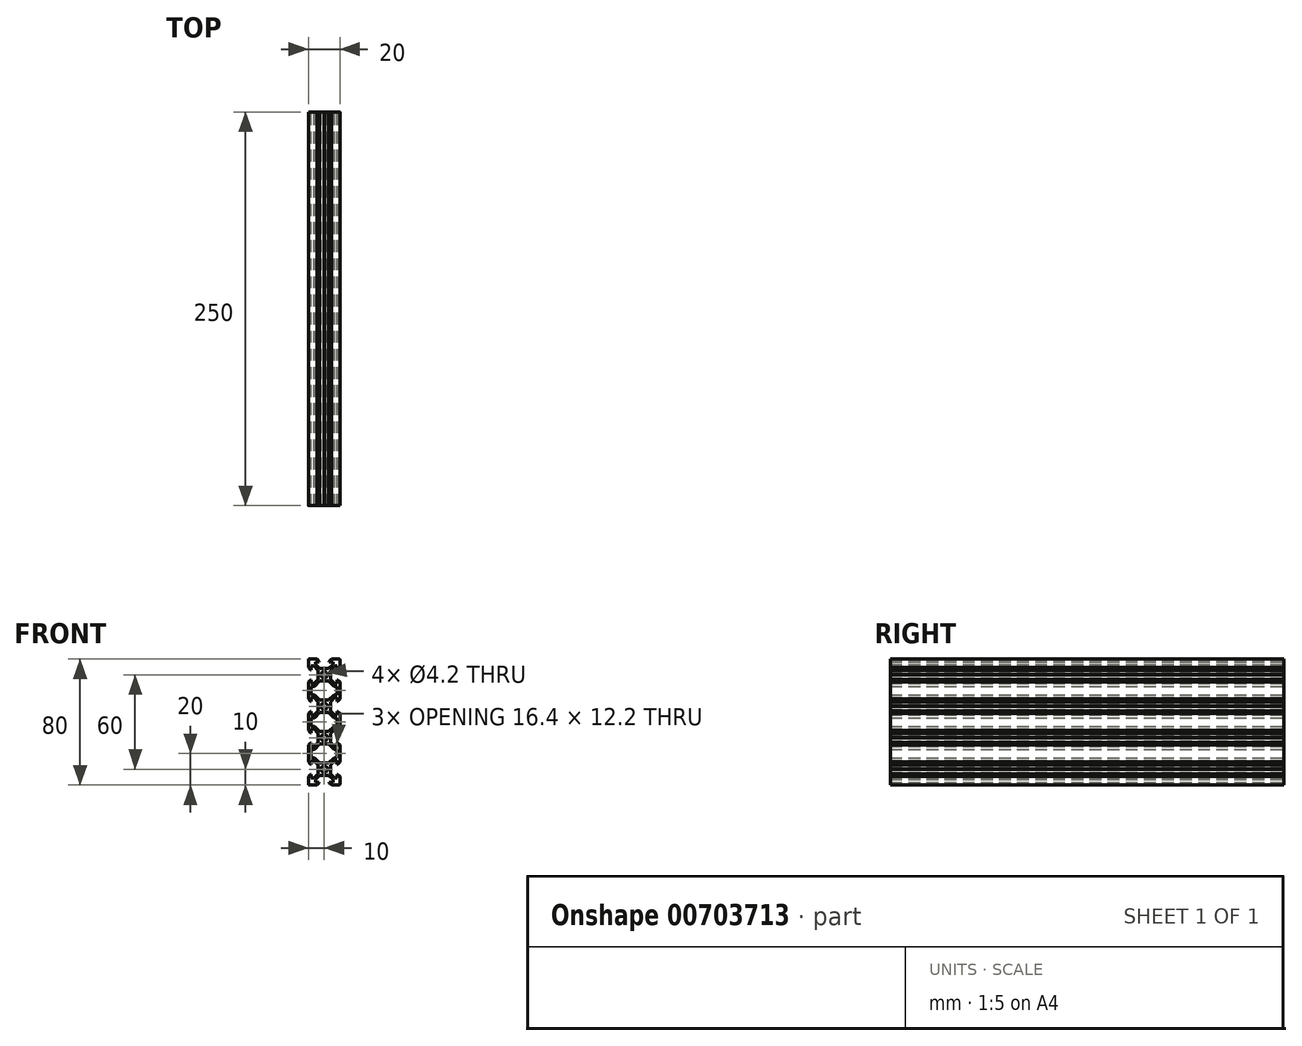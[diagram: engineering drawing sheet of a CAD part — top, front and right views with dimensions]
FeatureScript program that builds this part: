
annotation { "Feature Type Name" : "Feature", "Feature Type Description" : "" }
export const myFeature = defineFeature(function(context is Context, id is Id, definition is map)
    precondition{}
    {
        {
            var Q0;
            Q0=qCreatedBy(makeId("Front.planeOp"),FACE);
            var sketch = newSketch(context, id + "F0", { "sketchPlane" : qUnion([Q0])});
            skLineSegment(sketch, "E0", {"start": v(-3.9, 27.16) * mm, "end": v(-3.9, 29.79) * mm});
            skLineSegment(sketch, "E1", {"start": v(-6.56, 24.5) * mm, "end": v(-3.9, 27.16) * mm});
            skLineSegment(sketch, "E2", {"start": v(-8.2, 24.5) * mm, "end": v(-6.56, 24.5) * mm});
            skLineSegment(sketch, "E3", {"start": v(-8.2, 26.88) * mm, "end": v(-8.2, 24.5) * mm});
            skLineSegment(sketch, "E4", {"start": v(-8.54, 26.88) * mm, "end": v(-8.2, 26.88) * mm});
            skLineSegment(sketch, "E5", {"start": v(-10, 25.42) * mm, "end": v(-8.54, 26.88) * mm});
            skLineSegment(sketch, "E6", {"start": v(-10, 25.42) * mm, "end": v(-10, 14.58) * mm});
            skLineSegment(sketch, "E7", {"start": v(-10, 14.58) * mm, "end": v(-8.54, 13.12) * mm});
            skLineSegment(sketch, "E8", {"start": v(-8.54, 13.12) * mm, "end": v(-8.2, 13.12) * mm});
            skLineSegment(sketch, "E9", {"start": v(-8.2, 13.12) * mm, "end": v(-8.2, 15.5) * mm});
            skLineSegment(sketch, "E10", {"start": v(-8.2, 15.5) * mm, "end": v(-6.56, 15.5) * mm});
            skLineSegment(sketch, "E11", {"start": v(-6.56, 15.5) * mm, "end": v(-3.9, 12.84) * mm});
            skLineSegment(sketch, "E12", {"start": v(-3.9, 12.84) * mm, "end": v(-3.9, 10.21) * mm});
            skLineSegment(sketch, "E13", {"start": v(-3.9, 10.21) * mm, "end": v(-3.69, 10) * mm});
            skLineSegment(sketch, "E14", {"start": v(-3.9, 9.8) * mm, "end": v(-3.69, 10) * mm});
            skLineSegment(sketch, "E15", {"start": v(-3.9, 7.16) * mm, "end": v(-3.9, 9.8) * mm});
            skLineSegment(sketch, "E16", {"start": v(-6.56, 4.5) * mm, "end": v(-3.9, 7.16) * mm});
            skLineSegment(sketch, "E17", {"start": v(-8.2, 4.5) * mm, "end": v(-6.56, 4.5) * mm});
            skLineSegment(sketch, "E18", {"start": v(-8.2, 6.88) * mm, "end": v(-8.2, 4.5) * mm});
            skLineSegment(sketch, "E19", {"start": v(-8.54, 6.88) * mm, "end": v(-8.2, 6.88) * mm});
            skLineSegment(sketch, "E20", {"start": v(-10, 5.42) * mm, "end": v(-8.54, 6.88) * mm});
            skLineSegment(sketch, "E21", {"start": v(-10, 5.42) * mm, "end": v(-10, -5.42) * mm});
            skLineSegment(sketch, "E22", {"start": v(-10, -5.42) * mm, "end": v(-8.54, -6.88) * mm});
            skLineSegment(sketch, "E23", {"start": v(-8.54, -6.88) * mm, "end": v(-8.2, -6.88) * mm});
            skLineSegment(sketch, "E24", {"start": v(-8.2, -6.88) * mm, "end": v(-8.2, -4.5) * mm});
            skLineSegment(sketch, "E25", {"start": v(-8.2, -4.5) * mm, "end": v(-6.56, -4.5) * mm});
            skLineSegment(sketch, "E26", {"start": v(-6.56, -4.5) * mm, "end": v(-3.9, -7.16) * mm});
            skLineSegment(sketch, "E27", {"start": v(-3.9, -7.16) * mm, "end": v(-3.9, -9.8) * mm});
            skLineSegment(sketch, "E28", {"start": v(-3.9, -9.8) * mm, "end": v(-3.69, -10) * mm});
            skLineSegment(sketch, "E29", {"start": v(-3.9, -10.21) * mm, "end": v(-3.69, -10) * mm});
            skLineSegment(sketch, "E30", {"start": v(-3.9, -12.84) * mm, "end": v(-3.9, -10.21) * mm});
            skLineSegment(sketch, "E31", {"start": v(-6.56, -15.5) * mm, "end": v(-3.9, -12.84) * mm});
            skLineSegment(sketch, "E32", {"start": v(-8.2, -15.5) * mm, "end": v(-6.56, -15.5) * mm});
            skLineSegment(sketch, "E33", {"start": v(-8.2, -13.12) * mm, "end": v(-8.2, -15.5) * mm});
            skLineSegment(sketch, "E34", {"start": v(-8.54, -13.12) * mm, "end": v(-8.2, -13.12) * mm});
            skLineSegment(sketch, "E35", {"start": v(-10, -14.58) * mm, "end": v(-8.54, -13.12) * mm});
            skLineSegment(sketch, "E36", {"start": v(-10, -14.58) * mm, "end": v(-10, -25.42) * mm});
            skLineSegment(sketch, "E37", {"start": v(-10, -25.42) * mm, "end": v(-8.54, -26.88) * mm});
            skLineSegment(sketch, "E38", {"start": v(-8.54, -26.88) * mm, "end": v(-8.2, -26.88) * mm});
            skLineSegment(sketch, "E39", {"start": v(-8.2, -26.88) * mm, "end": v(-8.2, -24.5) * mm});
            skLineSegment(sketch, "E40", {"start": v(-8.2, -24.5) * mm, "end": v(-6.56, -24.5) * mm});
            skLineSegment(sketch, "E41", {"start": v(-6.56, -24.5) * mm, "end": v(-3.9, -27.16) * mm});
            skLineSegment(sketch, "E42", {"start": v(-3.9, -27.16) * mm, "end": v(-3.9, -29.79) * mm});
            skLineSegment(sketch, "E43", {"start": v(-3.9, -29.79) * mm, "end": v(-3.69, -30) * mm});
            skLineSegment(sketch, "E44", {"start": v(-3.9, -30.21) * mm, "end": v(-3.69, -30) * mm});
            skLineSegment(sketch, "E45", {"start": v(-3.9, -32.84) * mm, "end": v(-3.9, -30.21) * mm});
            skLineSegment(sketch, "E46", {"start": v(-6.56, -35.5) * mm, "end": v(-3.9, -32.84) * mm});
            skLineSegment(sketch, "E47", {"start": v(-8.2, -35.5) * mm, "end": v(-6.56, -35.5) * mm});
            skLineSegment(sketch, "E48", {"start": v(-8.2, -33.12) * mm, "end": v(-8.2, -35.5) * mm});
            skLineSegment(sketch, "E49", {"start": v(-8.54, -33.12) * mm, "end": v(-8.2, -33.12) * mm});
            skLineSegment(sketch, "E50", {"start": v(-10, -34.58) * mm, "end": v(-8.54, -33.12) * mm});
            skLineSegment(sketch, "E51", {"start": v(-10, -34.58) * mm, "end": v(-10, -39.5) * mm});
            skArc(sketch, "E52", {"start": v(-9.5, -40) * mm, "mid": v(-9.85, -39.85) * mm, "end": v(-10, -39.5) * mm});
            skLineSegment(sketch, "E53", {"start": v(-4.58, -40) * mm, "end": v(-9.5, -40) * mm});
            skLineSegment(sketch, "E54", {"start": v(-4.58, -40) * mm, "end": v(-3.12, -38.55) * mm});
            skLineSegment(sketch, "E55", {"start": v(-3.12, -38.55) * mm, "end": v(-3.12, -38.2) * mm});
            skLineSegment(sketch, "E56", {"start": v(-3.12, -38.2) * mm, "end": v(-5.5, -38.2) * mm});
            skLineSegment(sketch, "E57", {"start": v(-5.5, -38.2) * mm, "end": v(-5.5, -36.56) * mm});
            skLineSegment(sketch, "E58", {"start": v(-5.5, -36.56) * mm, "end": v(-2.84, -33.9) * mm});
            skLineSegment(sketch, "E59", {"start": v(-2.84, -33.9) * mm, "end": v(-0.21, -33.9) * mm});
            skLineSegment(sketch, "E60", {"start": v(-0.21, -33.9) * mm, "end": v(0, -33.69) * mm});
            skLineSegment(sketch, "E61", {"start": v(0.21, -33.9) * mm, "end": v(0, -33.69) * mm});
            skLineSegment(sketch, "E62", {"start": v(2.84, -33.9) * mm, "end": v(0.21, -33.9) * mm});
            skLineSegment(sketch, "E63", {"start": v(5.5, -36.56) * mm, "end": v(2.84, -33.9) * mm});
            skLineSegment(sketch, "E64", {"start": v(5.5, -38.2) * mm, "end": v(5.5, -36.56) * mm});
            skLineSegment(sketch, "E65", {"start": v(3.12, -38.2) * mm, "end": v(5.5, -38.2) * mm});
            skLineSegment(sketch, "E66", {"start": v(3.12, -38.55) * mm, "end": v(3.12, -38.2) * mm});
            skLineSegment(sketch, "E67", {"start": v(4.58, -40) * mm, "end": v(3.12, -38.55) * mm});
            skLineSegment(sketch, "E68", {"start": v(9.5, -40) * mm, "end": v(4.58, -40) * mm});
            skArc(sketch, "E69", {"start": v(10, -39.5) * mm, "mid": v(9.85, -39.85) * mm, "end": v(9.5, -40) * mm});
            skLineSegment(sketch, "E70", {"start": v(10, -34.58) * mm, "end": v(10, -39.5) * mm});
            skLineSegment(sketch, "E71", {"start": v(10, -34.58) * mm, "end": v(8.54, -33.12) * mm});
            skLineSegment(sketch, "E72", {"start": v(8.54, -33.12) * mm, "end": v(8.2, -33.12) * mm});
            skLineSegment(sketch, "E73", {"start": v(8.2, -33.12) * mm, "end": v(8.2, -35.5) * mm});
            skLineSegment(sketch, "E74", {"start": v(8.2, -35.5) * mm, "end": v(6.56, -35.5) * mm});
            skLineSegment(sketch, "E75", {"start": v(6.56, -35.5) * mm, "end": v(3.9, -32.84) * mm});
            skLineSegment(sketch, "E76", {"start": v(3.9, -32.84) * mm, "end": v(3.9, -30.21) * mm});
            skLineSegment(sketch, "E77", {"start": v(3.9, -30.21) * mm, "end": v(3.69, -30) * mm});
            skLineSegment(sketch, "E78", {"start": v(3.9, -29.79) * mm, "end": v(3.69, -30) * mm});
            skLineSegment(sketch, "E79", {"start": v(3.9, -27.16) * mm, "end": v(3.9, -29.79) * mm});
            skLineSegment(sketch, "E80", {"start": v(6.56, -24.5) * mm, "end": v(3.9, -27.16) * mm});
            skLineSegment(sketch, "E81", {"start": v(8.2, -24.5) * mm, "end": v(6.56, -24.5) * mm});
            skLineSegment(sketch, "E82", {"start": v(8.2, -26.88) * mm, "end": v(8.2, -24.5) * mm});
            skLineSegment(sketch, "E83", {"start": v(8.54, -26.88) * mm, "end": v(8.2, -26.88) * mm});
            skLineSegment(sketch, "E84", {"start": v(10, -25.42) * mm, "end": v(8.54, -26.88) * mm});
            skLineSegment(sketch, "E85", {"start": v(10, -14.58) * mm, "end": v(10, -25.42) * mm});
            skLineSegment(sketch, "E86", {"start": v(10, -14.58) * mm, "end": v(8.54, -13.12) * mm});
            skLineSegment(sketch, "E87", {"start": v(8.54, -13.12) * mm, "end": v(8.2, -13.12) * mm});
            skLineSegment(sketch, "E88", {"start": v(8.2, -13.12) * mm, "end": v(8.2, -15.5) * mm});
            skLineSegment(sketch, "E89", {"start": v(8.2, -15.5) * mm, "end": v(6.56, -15.5) * mm});
            skLineSegment(sketch, "E90", {"start": v(6.56, -15.5) * mm, "end": v(3.9, -12.84) * mm});
            skLineSegment(sketch, "E91", {"start": v(3.9, -12.84) * mm, "end": v(3.9, -10.21) * mm});
            skLineSegment(sketch, "E92", {"start": v(3.9, -10.21) * mm, "end": v(3.69, -10) * mm});
            skLineSegment(sketch, "E93", {"start": v(3.9, -9.8) * mm, "end": v(3.69, -10) * mm});
            skLineSegment(sketch, "E94", {"start": v(3.9, -7.16) * mm, "end": v(3.9, -9.8) * mm});
            skLineSegment(sketch, "E95", {"start": v(6.56, -4.5) * mm, "end": v(3.9, -7.16) * mm});
            skLineSegment(sketch, "E96", {"start": v(8.2, -4.5) * mm, "end": v(6.56, -4.5) * mm});
            skLineSegment(sketch, "E97", {"start": v(8.2, -6.88) * mm, "end": v(8.2, -4.5) * mm});
            skLineSegment(sketch, "E98", {"start": v(8.54, -6.88) * mm, "end": v(8.2, -6.88) * mm});
            skLineSegment(sketch, "E99", {"start": v(10, -5.42) * mm, "end": v(8.54, -6.88) * mm});
            skLineSegment(sketch, "E100", {"start": v(10, 5.42) * mm, "end": v(10, -5.42) * mm});
            skLineSegment(sketch, "E101", {"start": v(10, 5.42) * mm, "end": v(8.54, 6.88) * mm});
            skLineSegment(sketch, "E102", {"start": v(8.54, 6.88) * mm, "end": v(8.2, 6.88) * mm});
            skLineSegment(sketch, "E103", {"start": v(8.2, 6.88) * mm, "end": v(8.2, 4.5) * mm});
            skLineSegment(sketch, "E104", {"start": v(8.2, 4.5) * mm, "end": v(6.56, 4.5) * mm});
            skLineSegment(sketch, "E105", {"start": v(6.56, 4.5) * mm, "end": v(3.9, 7.16) * mm});
            skLineSegment(sketch, "E106", {"start": v(3.9, 7.16) * mm, "end": v(3.9, 9.8) * mm});
            skLineSegment(sketch, "E107", {"start": v(3.9, 9.8) * mm, "end": v(3.69, 10) * mm});
            skLineSegment(sketch, "E108", {"start": v(3.9, 10.21) * mm, "end": v(3.69, 10) * mm});
            skLineSegment(sketch, "E109", {"start": v(3.9, 12.84) * mm, "end": v(3.9, 10.21) * mm});
            skLineSegment(sketch, "E110", {"start": v(6.56, 15.5) * mm, "end": v(3.9, 12.84) * mm});
            skLineSegment(sketch, "E111", {"start": v(8.2, 15.5) * mm, "end": v(6.56, 15.5) * mm});
            skLineSegment(sketch, "E112", {"start": v(8.2, 13.12) * mm, "end": v(8.2, 15.5) * mm});
            skLineSegment(sketch, "E113", {"start": v(8.54, 13.12) * mm, "end": v(8.2, 13.12) * mm});
            skLineSegment(sketch, "E114", {"start": v(10, 14.58) * mm, "end": v(8.54, 13.12) * mm});
            skLineSegment(sketch, "E115", {"start": v(10, 25.42) * mm, "end": v(10, 14.58) * mm});
            skLineSegment(sketch, "E116", {"start": v(10, 25.42) * mm, "end": v(8.54, 26.88) * mm});
            skLineSegment(sketch, "E117", {"start": v(8.54, 26.88) * mm, "end": v(8.2, 26.88) * mm});
            skLineSegment(sketch, "E118", {"start": v(8.2, 26.88) * mm, "end": v(8.2, 24.5) * mm});
            skLineSegment(sketch, "E119", {"start": v(8.2, 24.5) * mm, "end": v(6.56, 24.5) * mm});
            skLineSegment(sketch, "E120", {"start": v(6.56, 24.5) * mm, "end": v(3.9, 27.16) * mm});
            skLineSegment(sketch, "E121", {"start": v(3.9, 27.16) * mm, "end": v(3.9, 29.79) * mm});
            skLineSegment(sketch, "E122", {"start": v(3.9, 29.79) * mm, "end": v(3.69, 30) * mm});
            skLineSegment(sketch, "E123", {"start": v(3.9, 30.21) * mm, "end": v(3.69, 30) * mm});
            skLineSegment(sketch, "E124", {"start": v(3.9, 32.84) * mm, "end": v(3.9, 30.21) * mm});
            skLineSegment(sketch, "E125", {"start": v(6.56, 35.5) * mm, "end": v(3.9, 32.84) * mm});
            skLineSegment(sketch, "E126", {"start": v(8.2, 35.5) * mm, "end": v(6.56, 35.5) * mm});
            skLineSegment(sketch, "E127", {"start": v(8.2, 33.12) * mm, "end": v(8.2, 35.5) * mm});
            skLineSegment(sketch, "E128", {"start": v(8.54, 33.12) * mm, "end": v(8.2, 33.12) * mm});
            skLineSegment(sketch, "E129", {"start": v(10, 34.58) * mm, "end": v(8.54, 33.12) * mm});
            skLineSegment(sketch, "E130", {"start": v(10, 39.5) * mm, "end": v(10, 34.58) * mm});
            skArc(sketch, "E131", {"start": v(9.5, 40) * mm, "mid": v(9.85, 39.85) * mm, "end": v(10, 39.5) * mm});
            skLineSegment(sketch, "E132", {"start": v(9.5, 40) * mm, "end": v(4.58, 40) * mm});
            skLineSegment(sketch, "E133", {"start": v(4.58, 40) * mm, "end": v(3.12, 38.55) * mm});
            skLineSegment(sketch, "E134", {"start": v(3.12, 38.55) * mm, "end": v(3.12, 38.2) * mm});
            skLineSegment(sketch, "E135", {"start": v(3.12, 38.2) * mm, "end": v(5.5, 38.2) * mm});
            skLineSegment(sketch, "E136", {"start": v(5.5, 38.2) * mm, "end": v(5.5, 36.56) * mm});
            skLineSegment(sketch, "E137", {"start": v(5.5, 36.56) * mm, "end": v(2.84, 33.9) * mm});
            skLineSegment(sketch, "E138", {"start": v(2.84, 33.9) * mm, "end": v(0.21, 33.9) * mm});
            skLineSegment(sketch, "E139", {"start": v(0.21, 33.9) * mm, "end": v(0, 33.69) * mm});
            skLineSegment(sketch, "E140", {"start": v(-0.21, 33.9) * mm, "end": v(0, 33.69) * mm});
            skLineSegment(sketch, "E141", {"start": v(-2.84, 33.9) * mm, "end": v(-0.21, 33.9) * mm});
            skLineSegment(sketch, "E142", {"start": v(-5.5, 36.56) * mm, "end": v(-2.84, 33.9) * mm});
            skLineSegment(sketch, "E143", {"start": v(-5.5, 38.2) * mm, "end": v(-5.5, 36.56) * mm});
            skLineSegment(sketch, "E144", {"start": v(-3.12, 38.2) * mm, "end": v(-5.5, 38.2) * mm});
            skLineSegment(sketch, "E145", {"start": v(-3.12, 38.55) * mm, "end": v(-3.12, 38.2) * mm});
            skLineSegment(sketch, "E146", {"start": v(-4.58, 40) * mm, "end": v(-3.12, 38.55) * mm});
            skLineSegment(sketch, "E147", {"start": v(-4.58, 40) * mm, "end": v(-9.5, 40) * mm});
            skArc(sketch, "E148", {"start": v(-10, 39.5) * mm, "mid": v(-9.85, 39.85) * mm, "end": v(-9.5, 40) * mm});
            skLineSegment(sketch, "E149", {"start": v(-10, 39.5) * mm, "end": v(-10, 34.58) * mm});
            skLineSegment(sketch, "E150", {"start": v(-10, 34.58) * mm, "end": v(-8.54, 33.12) * mm});
            skLineSegment(sketch, "E151", {"start": v(-8.54, 33.12) * mm, "end": v(-8.2, 33.12) * mm});
            skLineSegment(sketch, "E152", {"start": v(-8.2, 33.12) * mm, "end": v(-8.2, 35.5) * mm});
            skLineSegment(sketch, "E153", {"start": v(-8.2, 35.5) * mm, "end": v(-6.56, 35.5) * mm});
            skLineSegment(sketch, "E154", {"start": v(-6.56, 35.5) * mm, "end": v(-3.9, 32.84) * mm});
            skLineSegment(sketch, "E155", {"start": v(-3.9, 32.84) * mm, "end": v(-3.9, 30.21) * mm});
            skLineSegment(sketch, "E156", {"start": v(-3.9, 30.21) * mm, "end": v(-3.69, 30) * mm});
            skLineSegment(sketch, "E157", {"start": v(-3.9, 29.79) * mm, "end": v(-3.69, 30) * mm});
            skLineSegment(sketch, "E158", {"start": v(2.84, 13.9) * mm, "end": v(6.24, 17.3) * mm});
            skLineSegment(sketch, "E159", {"start": v(-2.84, 13.9) * mm, "end": v(2.84, 13.9) * mm});
            skLineSegment(sketch, "E160", {"start": v(-2.84, 13.9) * mm, "end": v(-6.24, 17.3) * mm});
            skLineSegment(sketch, "E161", {"start": v(-6.24, 17.3) * mm, "end": v(-8.2, 17.3) * mm});
            skLineSegment(sketch, "E162", {"start": v(-8.2, 22.7) * mm, "end": v(-8.2, 17.3) * mm});
            skLineSegment(sketch, "E163", {"start": v(-6.24, 22.7) * mm, "end": v(-8.2, 22.7) * mm});
            skLineSegment(sketch, "E164", {"start": v(-2.84, 26.1) * mm, "end": v(-6.24, 22.7) * mm});
            skLineSegment(sketch, "E165", {"start": v(-2.84, 26.1) * mm, "end": v(2.84, 26.1) * mm});
            skLineSegment(sketch, "E166", {"start": v(2.84, 26.1) * mm, "end": v(6.24, 22.7) * mm});
            skLineSegment(sketch, "E167", {"start": v(6.24, 22.7) * mm, "end": v(8.2, 22.7) * mm});
            skLineSegment(sketch, "E168", {"start": v(8.2, 22.7) * mm, "end": v(8.2, 17.3) * mm});
            skLineSegment(sketch, "E169", {"start": v(6.24, 17.3) * mm, "end": v(8.2, 17.3) * mm});
            skLineSegment(sketch, "E170", {"start": v(2.84, -6.1) * mm, "end": v(6.24, -2.7) * mm});
            skLineSegment(sketch, "E171", {"start": v(-2.84, -6.1) * mm, "end": v(2.84, -6.1) * mm});
            skLineSegment(sketch, "E172", {"start": v(-2.84, -6.1) * mm, "end": v(-6.24, -2.7) * mm});
            skLineSegment(sketch, "E173", {"start": v(-6.24, -2.7) * mm, "end": v(-8.2, -2.7) * mm});
            skLineSegment(sketch, "E174", {"start": v(-8.2, 2.7) * mm, "end": v(-8.2, -2.7) * mm});
            skLineSegment(sketch, "E175", {"start": v(-6.24, 2.7) * mm, "end": v(-8.2, 2.7) * mm});
            skLineSegment(sketch, "E176", {"start": v(-2.84, 6.1) * mm, "end": v(-6.24, 2.7) * mm});
            skLineSegment(sketch, "E177", {"start": v(-2.84, 6.1) * mm, "end": v(2.84, 6.1) * mm});
            skLineSegment(sketch, "E178", {"start": v(2.84, 6.1) * mm, "end": v(6.24, 2.7) * mm});
            skLineSegment(sketch, "E179", {"start": v(6.24, 2.7) * mm, "end": v(8.2, 2.7) * mm});
            skLineSegment(sketch, "E180", {"start": v(8.2, 2.7) * mm, "end": v(8.2, -2.7) * mm});
            skLineSegment(sketch, "E181", {"start": v(6.24, -2.7) * mm, "end": v(8.2, -2.7) * mm});
            skLineSegment(sketch, "E182", {"start": v(2.84, -26.1) * mm, "end": v(6.24, -22.7) * mm});
            skLineSegment(sketch, "E183", {"start": v(-2.84, -26.1) * mm, "end": v(2.84, -26.1) * mm});
            skLineSegment(sketch, "E184", {"start": v(-2.84, -26.1) * mm, "end": v(-6.24, -22.7) * mm});
            skLineSegment(sketch, "E185", {"start": v(-6.24, -22.7) * mm, "end": v(-8.2, -22.7) * mm});
            skLineSegment(sketch, "E186", {"start": v(-8.2, -17.3) * mm, "end": v(-8.2, -22.7) * mm});
            skLineSegment(sketch, "E187", {"start": v(-6.24, -17.3) * mm, "end": v(-8.2, -17.3) * mm});
            skLineSegment(sketch, "E188", {"start": v(-2.84, -13.9) * mm, "end": v(-6.24, -17.3) * mm});
            skLineSegment(sketch, "E189", {"start": v(-2.84, -13.9) * mm, "end": v(2.84, -13.9) * mm});
            skLineSegment(sketch, "E190", {"start": v(2.84, -13.9) * mm, "end": v(6.24, -17.3) * mm});
            skLineSegment(sketch, "E191", {"start": v(6.24, -17.3) * mm, "end": v(8.2, -17.3) * mm});
            skLineSegment(sketch, "E192", {"start": v(8.2, -17.3) * mm, "end": v(8.2, -22.7) * mm});
            skLineSegment(sketch, "E193", {"start": v(6.24, -22.7) * mm, "end": v(8.2, -22.7) * mm});
            skCircle(sketch, "E194", {"center": v(0, 10) * mm, "radius": 2.1 * mm});
            skCircle(sketch, "E195", {"center": v(0, 30) * mm, "radius": 2.1 * mm});
            skCircle(sketch, "E196", {"center": v(0, -30) * mm, "radius": 2.1 * mm});
            skCircle(sketch, "E197", {"center": v(0, -10) * mm, "radius": 2.1 * mm});
            skSolve(sketch);
        }
        {
            var Q0;
            Q0=makeQuery(id+"F0.imprint","IMPRINT",FACE,{"disambiguationData":[TD([[makeQuery(id+"F0.imprint","IMPRINT",EDGE,{"derivedFrom":sQuery(id+"F0.wireOp",EDGE,"E0")}),-1.0]])]});
            extrude(context, id + "F1", {"entities" : qUnion([Q0]), "depth" : 250 * mm, "offsetDistance" : 25 * mm});
        }
    });
